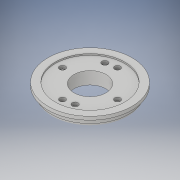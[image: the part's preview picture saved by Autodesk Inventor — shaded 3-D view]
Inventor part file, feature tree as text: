
AUTODESK INVENTOR PART (.ipt)
format: ipt  version: 2017 (Build 210142000, 142)  size: 184,832 bytes
history: native  units: in
note: dims shown in document units (in); Inventor stores cm internally (conversion verified against a paired STEP export)
features: sketch x4, hole x2, revolve x1, extrude x1, fillet x1
ambient origin geometry x8: Origin, YZ Plane, XZ Plane, XY Plane, X Axis, Y Axis, Z Axis, Center Point
bodies: Solid1 (feature_tree)
feature tree (9):
  revolve  "Revolution1"  [1 undecoded]
  extrude  "Extrusion1"  Depth=0.691in
  hole  "Hole2"  [1 undecoded]
  hole  "Hole3"  [1 undecoded]
  fillet  "Fillet1"  Radius=0.062in
  sketch  "Sketch1"  dims[d0=1.814in d1=0.5in]
  sketch  "Sketch2"  dims[d2=0.691in d3=0.147in]
  sketch  "Sketch4"  dims[d4=1.668in d6=0.195in]
  sketch  "Sketch5"  dims[d10=90.0deg d11=3.0in d12=0.062in d13=0.0in d14=0.939in d15=0.0984in d25=2.376in d27=22.5deg d28=0.134in d29=0.75in d30=0.256in d31=0.134in d32=0.5635in d33=1.0in d34=0.8108in d35=2.376in d36=0.25in d37=0.75in d38=0.256in d39=0.134in d40=0.5635in d41=0.3in d42=0.0in d43=0.125in]
note: 3 required parameter values undecoded (feature->parameter linkage not recoverable at this tier; creation-order binding heuristic only, values carry confidence <= 0.55)